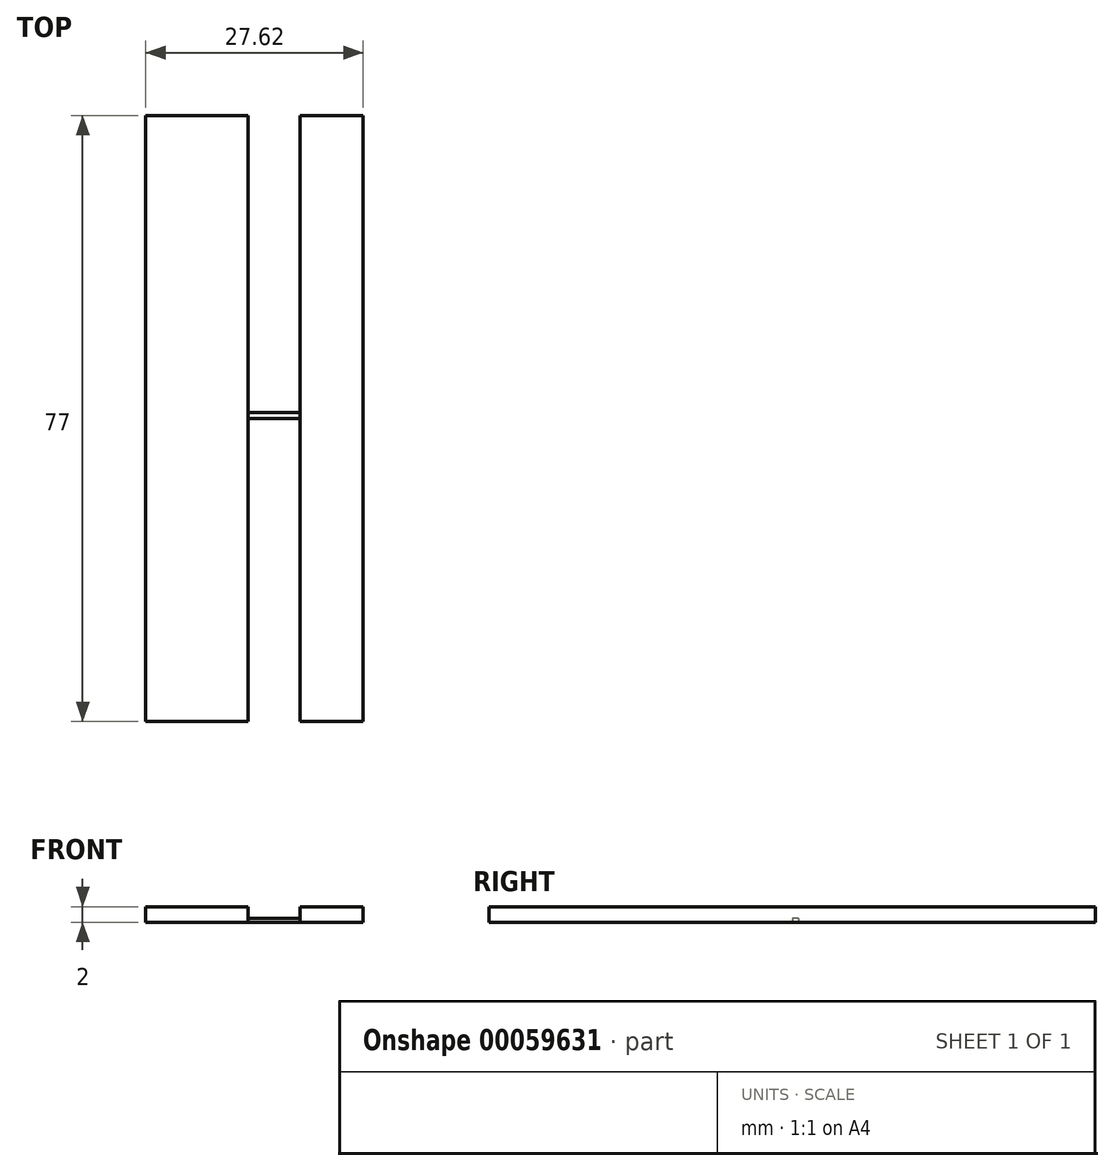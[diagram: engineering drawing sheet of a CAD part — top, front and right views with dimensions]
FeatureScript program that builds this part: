
annotation { "Feature Type Name" : "Feature", "Feature Type Description" : "" }
export const myFeature = defineFeature(function(context is Context, id is Id, definition is map)
    precondition{}
    {
        {
            var Q0;
            Q0=qCreatedBy(makeId("Top.planeOp"),FACE);
            var sketch = newSketch(context, id + "F0", { "sketchPlane" : qUnion([Q0])});
            skLineSegment(sketch, "E0.bottom", {"start": v(-80.65, 32.12) * mm, "end": v(-67.65, 32.12) * mm});
            skLineSegment(sketch, "E0.top", {"start": v(-80.65, -44.88) * mm, "end": v(-67.65, -44.88) * mm});
            skLineSegment(sketch, "E0.left", {"start": v(-80.65, 32.12) * mm, "end": v(-80.65, -44.88) * mm});
            skLineSegment(sketch, "E0.right", {"start": v(-67.65, 32.12) * mm, "end": v(-67.65, -44.88) * mm});
            skLineSegment(sketch, "E1.bottom", {"start": v(-61.03, 32.12) * mm, "end": v(-53.03, 32.12) * mm});
            skLineSegment(sketch, "E1.top", {"start": v(-61.03, -44.88) * mm, "end": v(-53.03, -44.88) * mm});
            skLineSegment(sketch, "E1.left", {"start": v(-61.03, 32.12) * mm, "end": v(-61.03, -44.88) * mm});
            skLineSegment(sketch, "E1.right", {"start": v(-53.03, 32.12) * mm, "end": v(-53.03, -44.88) * mm});
            skLineSegment(sketch, "E2.bottom", {"start": v(-67.65, -5.58) * mm, "end": v(-61.03, -5.58) * mm});
            skLineSegment(sketch, "E2.top", {"start": v(-67.65, -6.38) * mm, "end": v(-61.03, -6.38) * mm});
            skLineSegment(sketch, "E2.left", {"start": v(-67.65, -5.58) * mm, "end": v(-67.65, -6.38) * mm});
            skLineSegment(sketch, "E2.right", {"start": v(-61.03, -5.58) * mm, "end": v(-61.03, -6.38) * mm});
            skSolve(sketch);
        }
        {
            var Q0;
            Q0=makeQuery(id+"F0.imprint","IMPRINT",FACE,{"disambiguationData":[TD([[makeQuery(id+"F0.imprint","IMPRINT",EDGE,{"derivedFrom":sQuery(id+"F0.wireOp",EDGE,"E2.bottom")}),-1.0]])]});
            extrude(context, id + "F1", {"entities" : qUnion([Q0]), "depth" : 0.5 * mm});
        }
        {
            var Q0;
            {var subQ1=sQuery(id+"F0.wireOp",EDGE,"E0.bottom");Q0=makeQuery(id+"F0.imprint","IMPRINT",FACE,{"disambiguationData":[TD([[makeQuery(id+"F0.imprint","IMPRINT",EDGE,{"derivedFrom":subQ1}),-1.0]])]});}
            var Q1;
            {var subQ3=sQuery(id+"F0.wireOp",EDGE,"E1.bottom");Q1=makeQuery(id+"F0.imprint","IMPRINT",FACE,{"disambiguationData":[TD([[makeQuery(id+"F0.imprint","IMPRINT",EDGE,{"derivedFrom":subQ3}),-1.0]])]});}
            extrude(context, id + "F2", {"entities" : qUnion([Q0, Q1]), "operationType" : NewBodyOperationType.ADD, "depth" : 2 * mm});
        }
    });
